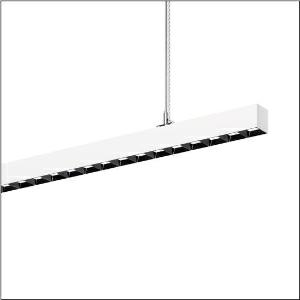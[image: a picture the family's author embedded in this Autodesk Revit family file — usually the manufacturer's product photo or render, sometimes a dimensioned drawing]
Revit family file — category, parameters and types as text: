
# Revit family: silica_r__21_51mx31dc4dwb_7dad
name_source: partatom
category: Lighting Fixtures
units: mm (PartAtom-declared; Revit-internal decimal feet)

## family parameters
Cut with Voids When Loaded = No
Host = Face
Light Source = No
Part Type = Normal
Room Calculation Point = No
Round Connector Dimension = Use Diameter
Shared = No

## types (1)
- --- (1 x LED, 18230 lm, 105.9 W, 4000K)
    Apparent Load = 106 VA
    CIE Flux Codes = 87 99 100 59 100
    Color Rendering = 80
    Color Temperature = 4000K
    Default Elevation = 1800 mm
    Description = Silica® 21, office luminaire, primary light control with darklight reflector, of PMMA, black, CAT 2 (L<= 3000cd/m²), light emission: direct/indirect distribution, primary light characteristic: symmetric, installation type: suspended mounting, LED, rated luminous flux: 18.230lm, luminous efficacy: 172lm/W, light colour: 840, colour temperature: 4000K, with terminal, 3+2-pole, max. 2.5mm², mains connection: 220..240V, AC, 50/60Hz, rated input power: 105.9W, luminaire housing, of aluminium, traffic white (RAL 9016), length: 3.004mm, width: 53mm, height: 53mm, protection rating (complete): IP20, insulation class (complete): insulation class I (protective earthing), certification: CE, permissible operating ambient temperature: 0..+35°C, standard: EN 50419, packaging unit: 1 piece
    Height = 53 mm
    Lamp = 1 x LED
    Lamp Light Flux = 18230 lm
    Lamp Power = 105.9 W
    Lamp count = 1
    Length = 3004 mm
    Luminous efficacy = 172 lm/W
    Manufacturer = Siteco
    ModVariant = No
    Model = 51MX31DC4DWB
    Mounting Place = Ceiling
    Mounting Type = Pendant
    Number of Poles = 1
    OnlyDefault = Yes
    Power Factor = 1
    Product Name = Silica® 21
    Product group = office luminaire | ceiling pendant
    ProductGroupID = 902
    Protection Class = Protection class I
    Protection Degree = IP 20
    RLX_Detail_Level = 1
    RLX_Emergency_Light_Flux = 0 lm
    RLX_Emergency_Type = 0
    RLX_Emergency_Type_DB = No
    RlxData = <blob elided: 64925 chars, md5=d9d291da>
    Socket = socket
    Standby Power = 0 W
    System Light Flux = 18230 lm
    System Power = 106 W
    Type Comments = factory setting: luminous flux: 100 % | dim-lin: 254 | 367 mA
    Type Image = l_1313619.jpg
    URL = http://relux.com
    VarID = @adj_070081
    Voltage = 0 V
    Weight = 0.00 kg
    Width = 53 mm

## geometry (parser evidence)
native form markers: Blend x4, Sweep x13
no freeform markers — native parametric forms only
